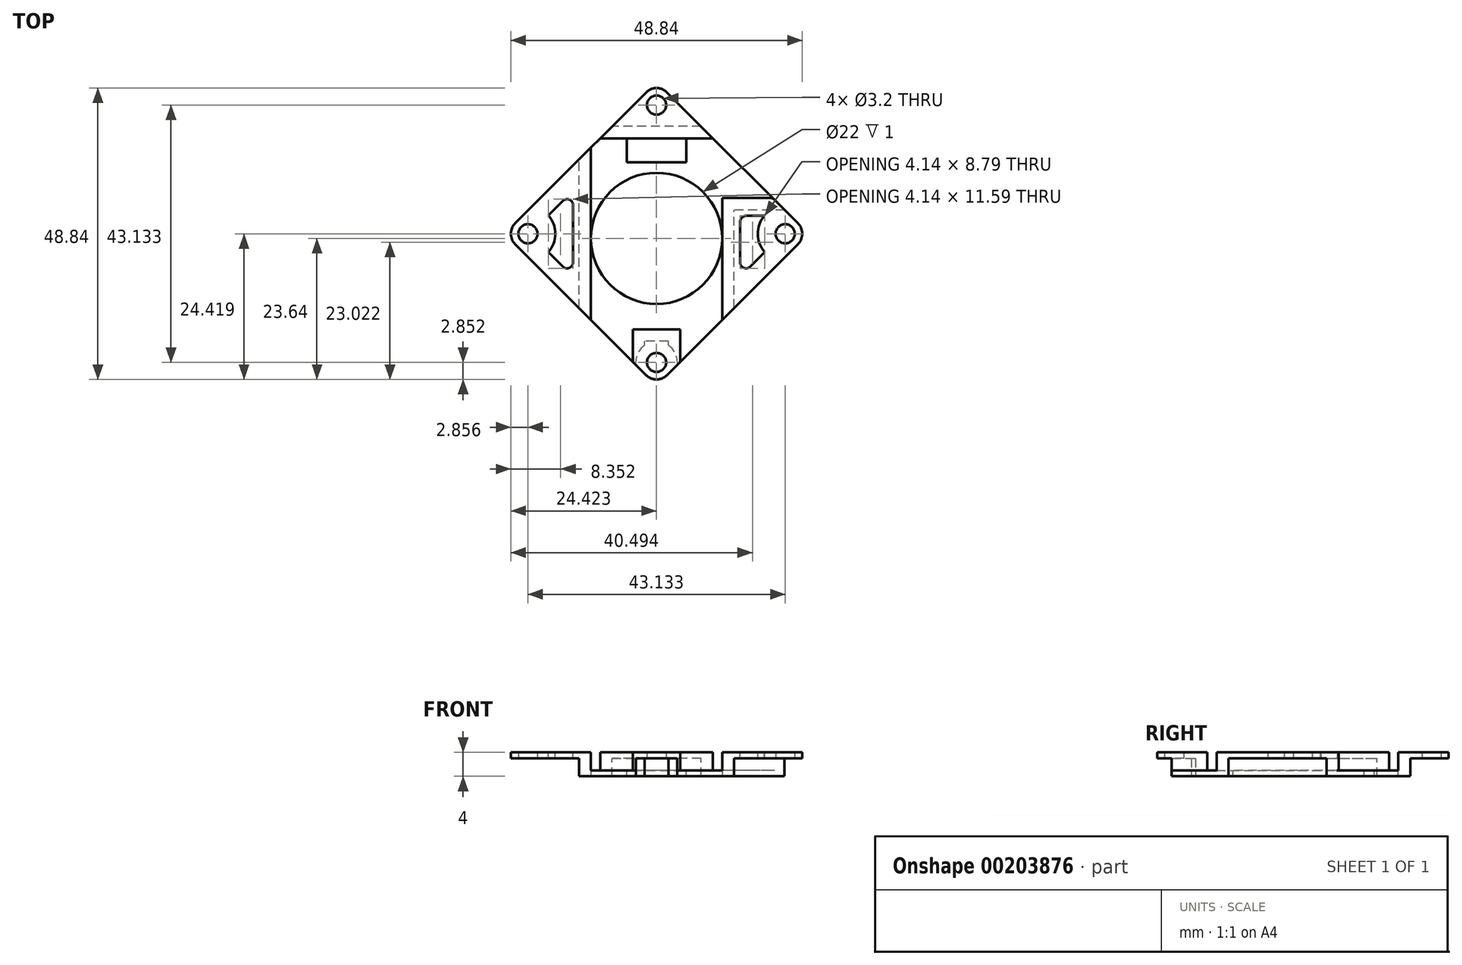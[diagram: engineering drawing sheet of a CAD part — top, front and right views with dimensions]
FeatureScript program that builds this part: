
annotation { "Feature Type Name" : "Feature", "Feature Type Description" : "" }
export const myFeature = defineFeature(function(context is Context, id is Id, definition is map)
    precondition{}
    {
        {
            var Q0;
            Q0=qCreatedBy(makeId("Top.planeOp"),FACE);
            var sketch = newSketch(context, id + "F0", { "sketchPlane" : qUnion([Q0])});
            skLineSegment(sketch, "E0.bottom", {"start": v(16.23, -22.9) * mm, "end": v(-14.77, -22.9) * mm});
            skLineSegment(sketch, "E0.top", {"start": v(16.23, 13.1) * mm, "end": v(-14.77, 13.1) * mm});
            skLineSegment(sketch, "E0.left", {"start": v(18.73, -20.4) * mm, "end": v(18.73, 10.6) * mm});
            skLineSegment(sketch, "E0.right", {"start": v(-17.27, -20.4) * mm, "end": v(-17.27, 10.6) * mm});
            skPoint(sketch, "E0.middle", {"position": v(0.73, -4.9) * mm});
            skCircle(sketch, "E1", {"center": v(-14.52, 10.34) * mm, "radius": 1.6 * mm});
            skPoint(sketch, "E2.visualSharp", {"position": v(-17.27, 13.1) * mm});
            skArc(sketch, "E2.filletArc", {"start": v(-14.77, 13.1) * mm, "mid": v(-16.53, 12.36) * mm, "end": v(-17.27, 10.6) * mm});
            skPoint(sketch, "E3.visualSharp", {"position": v(18.73, 13.1) * mm});
            skArc(sketch, "E3.filletArc", {"start": v(18.73, 10.6) * mm, "mid": v(18, 12.36) * mm, "end": v(16.23, 13.1) * mm});
            skPoint(sketch, "E4.visualSharp", {"position": v(18.73, -22.9) * mm});
            skArc(sketch, "E4.filletArc", {"start": v(16.23, -22.9) * mm, "mid": v(18, -22.18) * mm, "end": v(18.73, -20.4) * mm});
            skPoint(sketch, "E5.visualSharp", {"position": v(-17.27, -22.9) * mm});
            skArc(sketch, "E5.filletArc", {"start": v(-17.27, -20.4) * mm, "mid": v(-16.53, -22.18) * mm, "end": v(-14.77, -22.9) * mm});
            skCircle(sketch, "E6.0.1.0", {"center": v(-14.52, -20.16) * mm, "radius": 1.6 * mm});
            skCircle(sketch, "E6.1.0.0", {"center": v(15.98, 10.34) * mm, "radius": 1.6 * mm});
            skCircle(sketch, "E6.1.1.0", {"center": v(15.98, -20.16) * mm, "radius": 1.6 * mm});
            skLineSegment(sketch, "E6.direction1", {"start": v(-14.52, 10.34) * mm, "end": v(15.98, 10.34) * mm, "construction": true});
            skLineSegment(sketch, "E6.direction2", {"start": v(-14.52, 10.34) * mm, "end": v(-14.52, -20.16) * mm, "construction": true});
            skSolve(sketch);
        }
        {
            var Q0;
            Q0=makeQuery(id+"F0.imprint","IMPRINT",FACE,{"disambiguationData":[TD([[makeQuery(id+"F0.imprint","IMPRINT",EDGE,{"derivedFrom":sQuery(id+"F0.wireOp",EDGE,"E0.bottom")}),-1.0]])]});
            extrude(context, id + "F1", {"entities" : qUnion([Q0]), "depth" : 1 * mm});
        }
        {
            var Q0;
            Q0=makeQuery(id+"F1.opExtrude","SWEPT_BODY",BODY,{"disambiguationData":[OSD([sQuery(id+"F0.wireOp",EDGE,"E0.bottom"),sQuery(id+"F0.wireOp",EDGE,"E0.top"),sQuery(id+"F0.wireOp",EDGE,"E0.left"),sQuery(id+"F0.wireOp",EDGE,"E0.right"),sQuery(id+"F0.wireOp",EDGE,"E1"),sQuery(id+"F0.wireOp",EDGE,"E2.filletArc"),sQuery(id+"F0.wireOp",EDGE,"E3.filletArc"),sQuery(id+"F0.wireOp",EDGE,"E4.filletArc"),sQuery(id+"F0.wireOp",EDGE,"E5.filletArc"),sQuery(id+"F0.wireOp",EDGE,"E6.0.1.0"),sQuery(id+"F0.wireOp",EDGE,"E6.1.0.0"),sQuery(id+"F0.wireOp",EDGE,"E6.1.1.0")])]});
            var Q1;
            Q1=makeQuery(id+"F1.opExtrude","SWEPT_EDGE",EDGE,{"disambiguationData":[OSD([sQuery(id+"F0.wireOp",EDGE,"E0.bottom"),sQuery(id+"F0.wireOp",EDGE,"E4.filletArc")])]});
            transform(context, id + "F2", {"entities" : qUnion([Q0]), "transformType" : TransformType.ROTATION, "transformAxis" : qUnion([Q1]), "angle" : 45 * degree, "makeCopy" : false});
        }
        {
            var Q0;
            Q0=makeQuery(id+"F1.opExtrude","CAP_FACE",FACE,{"disambiguationData":[OSD([sQuery(id+"F0.wireOp",EDGE,"E0.bottom"),sQuery(id+"F0.wireOp",EDGE,"E0.top"),sQuery(id+"F0.wireOp",EDGE,"E0.left"),sQuery(id+"F0.wireOp",EDGE,"E0.right"),sQuery(id+"F0.wireOp",EDGE,"E1"),sQuery(id+"F0.wireOp",EDGE,"E2.filletArc"),sQuery(id+"F0.wireOp",EDGE,"E3.filletArc"),sQuery(id+"F0.wireOp",EDGE,"E4.filletArc"),sQuery(id+"F0.wireOp",EDGE,"E5.filletArc"),sQuery(id+"F0.wireOp",EDGE,"E6.0.1.0"),sQuery(id+"F0.wireOp",EDGE,"E6.1.0.0"),sQuery(id+"F0.wireOp",EDGE,"E6.1.1.0")])],"isStart":false});
            var sketch = newSketch(context, id + "F19", { "sketchPlane" : qUnion([Q0])});
            skLineSegment(sketch, "E7", {"start": v(18, 22.35) * mm, "end": v(18, -20.79) * mm, "construction": true});
            skLineSegment(sketch, "E8", {"start": v(-3.56, 0.78) * mm, "end": v(39.57, 0.78) * mm, "construction": true});
            skLineSegment(sketch, "E9.bottom", {"start": v(31, -17.22) * mm, "end": v(5, -17.22) * mm});
            skLineSegment(sketch, "E9.top", {"start": v(31, 18.78) * mm, "end": v(5, 18.78) * mm});
            skLineSegment(sketch, "E9.left", {"start": v(31, -17.22) * mm, "end": v(31, 18.78) * mm});
            skLineSegment(sketch, "E9.right", {"start": v(5, -17.22) * mm, "end": v(5, 18.78) * mm});
            skPoint(sketch, "E9.middle", {"position": v(18, 0.78) * mm});
            skSolve(sketch);
        }
        {
            var Q0;
            {var subQ6=makeQuery(id+"F1.opExtrude","CAP_EDGE",EDGE,{"disambiguationData":[OSD([sQuery(id+"F0.wireOp",EDGE,"E0.left")])],"isStart":false});var subQ13=sQuery(id+"F19.wireOp",EDGE,"E9.bottom");var subQ14=makeQuery(id+"F19.imprint","INTERSECT",VERTEX,{"derivedFrom":[subQ6,subQ13]});Q0=makeQuery(id+"F19.imprint","IMPRINT",FACE,{"disambiguationData":[TD([[makeQuery(id+"F19.imprint","IMPRINT",EDGE,{"disambiguationData":[TD([[subQ14,-1.0]])],"derivedFrom":subQ13}),-1.0]])]});}
            extrude(context, id + "F3", {"entities" : qUnion([Q0]), "operationType" : NewBodyOperationType.ADD, "oppositeDirection" : true, "depth" : 4 * mm});
        }
        {
            var Q0;
            Q0=makeQuery(id+"F1.opExtrude","CAP_FACE",FACE,{"disambiguationData":[OSD([sQuery(id+"F0.wireOp",EDGE,"E0.bottom"),sQuery(id+"F0.wireOp",EDGE,"E0.top"),sQuery(id+"F0.wireOp",EDGE,"E0.left"),sQuery(id+"F0.wireOp",EDGE,"E0.right"),sQuery(id+"F0.wireOp",EDGE,"E1"),sQuery(id+"F0.wireOp",EDGE,"E2.filletArc"),sQuery(id+"F0.wireOp",EDGE,"E3.filletArc"),sQuery(id+"F0.wireOp",EDGE,"E4.filletArc"),sQuery(id+"F0.wireOp",EDGE,"E5.filletArc"),sQuery(id+"F0.wireOp",EDGE,"E6.0.1.0"),sQuery(id+"F0.wireOp",EDGE,"E6.1.0.0"),sQuery(id+"F0.wireOp",EDGE,"E6.1.1.0")])],"isStart":false});
            var sketch = newSketch(context, id + "F4", { "sketchPlane" : qUnion([Q0])});
            skLineSegment(sketch, "E10", {"start": v(18, 22.35) * mm, "end": v(18, -20.79) * mm, "construction": true});
            skLineSegment(sketch, "E11.bottom", {"start": v(29, -15.22) * mm, "end": v(7, -15.22) * mm});
            skLineSegment(sketch, "E11.top", {"start": v(29, 16.78) * mm, "end": v(7, 16.78) * mm});
            skLineSegment(sketch, "E11.left", {"start": v(29, -15.22) * mm, "end": v(29, 16.78) * mm});
            skLineSegment(sketch, "E11.right", {"start": v(7, -15.22) * mm, "end": v(7, 16.78) * mm});
            skPoint(sketch, "E11.middle", {"position": v(18, 0.78) * mm});
            skSolve(sketch);
        }
        {
            var Q0;
            {var subQ6=makeQuery(id+"F1.opExtrude","CAP_EDGE",EDGE,{"disambiguationData":[OSD([sQuery(id+"F0.wireOp",EDGE,"E0.left")])],"isStart":false});var subQ13=sQuery(id+"F4.wireOp",EDGE,"E11.bottom");var subQ14=makeQuery(id+"F4.imprint","INTERSECT",VERTEX,{"derivedFrom":[subQ6,subQ13]});Q0=makeQuery(id+"F4.imprint","IMPRINT",FACE,{"disambiguationData":[TD([[makeQuery(id+"F4.imprint","IMPRINT",EDGE,{"disambiguationData":[TD([[subQ14,-1.0]])],"derivedFrom":subQ13}),-1.0]])]});}
            extrude(context, id + "F5", {"entities" : qUnion([Q0]), "operationType" : NewBodyOperationType.REMOVE, "oppositeDirection" : true, "depth" : 3 * mm});
        }
        {
            var Q0;
            {var subQ0=sQuery(id+"F0.wireOp",EDGE,"E6.1.1.0");var subQ1=sQuery(id+"F0.wireOp",EDGE,"E4.filletArc");var subQ2=sQuery(id+"F0.wireOp",EDGE,"E0.bottom");var subQ3=sQuery(id+"F0.wireOp",EDGE,"E0.left");Q0=makeQuery(id+"F5.boolean.opBoolean","SPLIT",FACE,{"disambiguationData":[TD([makeQuery(id+"F1.opExtrude","SWEPT_FACE",FACE,{"disambiguationData":[OSD([subQ1])]})])],"derivedFrom":makeQuery(id+"F1.opExtrude","CAP_FACE",FACE,{"disambiguationData":[OSD([subQ2,sQuery(id+"F0.wireOp",EDGE,"E0.top"),subQ3,sQuery(id+"F0.wireOp",EDGE,"E0.right"),sQuery(id+"F0.wireOp",EDGE,"E1"),sQuery(id+"F0.wireOp",EDGE,"E2.filletArc"),sQuery(id+"F0.wireOp",EDGE,"E3.filletArc"),subQ1,sQuery(id+"F0.wireOp",EDGE,"E5.filletArc"),sQuery(id+"F0.wireOp",EDGE,"E6.0.1.0"),sQuery(id+"F0.wireOp",EDGE,"E6.1.0.0"),subQ0])],"isStart":false})});}
            var sketch = newSketch(context, id + "F6", { "sketchPlane" : qUnion([Q0])});
            skLineSegment(sketch, "E12", {"start": v(14, -15.22) * mm, "end": v(14, -20.68) * mm});
            skLineSegment(sketch, "E13", {"start": v(18, -20.79) * mm, "end": v(18, -15.22) * mm, "construction": true});
            skLineSegment(sketch, "E14.MirrorCS", {"start": v(22, -15.22) * mm, "end": v(22, -20.68) * mm});
            skSolve(sketch);
        }
        {
            var Q0;
            {var subQ0=sQuery(id+"F6.wireOp",EDGE,"E12");Q0=makeQuery(id+"F6.imprint","IMPRINT",FACE,{"disambiguationData":[TD([[makeQuery(id+"F6.imprint","IMPRINT",EDGE,{"derivedFrom":subQ0}),-1.0]])]});}
            var Q1;
            {var subQ0=sQuery(id+"F6.wireOp",EDGE,"E14.MirrorCS");Q1=makeQuery(id+"F6.imprint","IMPRINT",FACE,{"disambiguationData":[TD([[makeQuery(id+"F6.imprint","IMPRINT",EDGE,{"derivedFrom":subQ0}),1.0]])]});}
            var Q2;
            Q2=makeQuery(id+"F5.boolean.opBoolean","COPY",FACE,{"derivedFrom":makeQuery(id+"F5.opExtrude","CAP_FACE",FACE,{"disambiguationData":[OSD([sQuery(id+"F0.wireOp",EDGE,"E0.bottom"),sQuery(id+"F0.wireOp",EDGE,"E0.top"),sQuery(id+"F0.wireOp",EDGE,"E0.left"),sQuery(id+"F0.wireOp",EDGE,"E0.right"),sQuery(id+"F4.wireOp",EDGE,"E11.bottom"),sQuery(id+"F4.wireOp",EDGE,"E11.top"),sQuery(id+"F4.wireOp",EDGE,"E11.left"),sQuery(id+"F4.wireOp",EDGE,"E11.right")])],"isStart":false})});
            extrude(context, id + "F20", {"entities" : qUnion([Q0, Q1]), "operationType" : NewBodyOperationType.REMOVE, "endBound" : BoundingType.UP_TO_SURFACE, "oppositeDirection" : true, "endBoundEntityFace" : qUnion([Q2]), "depth" : 25 * mm});
        }
        {
            var Q0;
            Q0=makeQuery(id+"F3.opExtrude","CAP_FACE",FACE,{"disambiguationData":[OSD([sQuery(id+"F0.wireOp",EDGE,"E0.bottom"),sQuery(id+"F0.wireOp",EDGE,"E0.top"),sQuery(id+"F0.wireOp",EDGE,"E0.left"),sQuery(id+"F0.wireOp",EDGE,"E0.right"),sQuery(id+"F19.wireOp",EDGE,"E9.bottom"),sQuery(id+"F19.wireOp",EDGE,"E9.top"),sQuery(id+"F19.wireOp",EDGE,"E9.left"),sQuery(id+"F19.wireOp",EDGE,"E9.right")])],"isStart":false});
            var sketch = newSketch(context, id + "F7", { "sketchPlane" : qUnion([Q0])});
            skLineSegment(sketch, "E15", {"start": v(18, 17.22) * mm, "end": v(18, -18.78) * mm, "construction": true});
            skCircle(sketch, "E16", {"center": v(18, 0) * mm, "radius": 11 * mm});
            skSolve(sketch);
        }
        {
            var Q0;
            Q0=makeQuery(id+"F7.imprint","IMPRINT",FACE,{"disambiguationData":[TD([[makeQuery(id+"F7.imprint","IMPRINT",EDGE,{"derivedFrom":sQuery(id+"F7.wireOp",EDGE,"E16")}),1.0]])]});
            extrude(context, id + "F8", {"entities" : qUnion([Q0]), "operationType" : NewBodyOperationType.REMOVE, "oppositeDirection" : true, "depth" : 25 * mm});
        }
        {
            var Q0;
            {var subQ0=sQuery(id+"F0.wireOp",EDGE,"E6.1.0.0");var subQ1=sQuery(id+"F0.wireOp",EDGE,"E0.left");var subQ2=sQuery(id+"F0.wireOp",EDGE,"E3.filletArc");var subQ3=sQuery(id+"F0.wireOp",EDGE,"E0.top");Q0=makeQuery(id+"F5.boolean.opBoolean","SPLIT",FACE,{"disambiguationData":[TD([makeQuery(id+"F1.opExtrude","SWEPT_FACE",FACE,{"disambiguationData":[OSD([subQ2])]})])],"derivedFrom":makeQuery(id+"F1.opExtrude","CAP_FACE",FACE,{"disambiguationData":[OSD([sQuery(id+"F0.wireOp",EDGE,"E0.bottom"),subQ3,subQ1,sQuery(id+"F0.wireOp",EDGE,"E0.right"),sQuery(id+"F0.wireOp",EDGE,"E1"),sQuery(id+"F0.wireOp",EDGE,"E2.filletArc"),subQ2,sQuery(id+"F0.wireOp",EDGE,"E4.filletArc"),sQuery(id+"F0.wireOp",EDGE,"E5.filletArc"),sQuery(id+"F0.wireOp",EDGE,"E6.0.1.0"),subQ0,sQuery(id+"F0.wireOp",EDGE,"E6.1.1.0")])],"isStart":false})});}
            var sketch = newSketch(context, id + "F21", { "sketchPlane" : qUnion([Q0])});
            skLineSegment(sketch, "E17", {"start": v(29, 6.78) * mm, "end": v(37.46, 6.78) * mm});
            skSolve(sketch);
        }
        {
            var Q0;
            {var subQ0=sQuery(id+"F21.wireOp",EDGE,"E17");Q0=makeQuery(id+"F21.imprint","IMPRINT",FACE,{"disambiguationData":[TD([[makeQuery(id+"F21.imprint","IMPRINT",EDGE,{"derivedFrom":subQ0}),1.0]])]});}
            var Q1;
            {var subQ0=sQuery(id+"F4.wireOp",EDGE,"E11.bottom");var subQ1=sQuery(id+"F0.wireOp",EDGE,"E0.bottom");var subQ2=sQuery(id+"F4.wireOp",EDGE,"E11.right");var subQ3=sQuery(id+"F4.wireOp",EDGE,"E11.left");var subQ4=sQuery(id+"F4.wireOp",EDGE,"E11.top");var subQ5=sQuery(id+"F0.wireOp",EDGE,"E0.right");var subQ6=sQuery(id+"F0.wireOp",EDGE,"E0.left");var subQ7=sQuery(id+"F0.wireOp",EDGE,"E0.top");var subQ8=makeQuery(id+"F20.opExtrude","CAP_FACE",FACE,{"disambiguationData":[OSD([subQ1,subQ7,subQ6,subQ5,subQ0,subQ4,subQ3,subQ2]),ownerDisambiguation([makeQuery(id+"F20.opExtrude","SWEPT_BODY",BODY,{"disambiguationData":[OSD([subQ1,subQ0,sQuery(id+"F6.wireOp",EDGE,"E12")])]})])],"isStart":false});var subQ9=makeQuery(id+"F20.opExtrude","CAP_FACE",FACE,{"disambiguationData":[OSD([subQ1,subQ7,subQ6,subQ5,subQ0,subQ4,subQ3,subQ2]),ownerDisambiguation([makeQuery(id+"F20.opExtrude","SWEPT_BODY",BODY,{"disambiguationData":[OSD([subQ6,subQ0,sQuery(id+"F6.wireOp",EDGE,"E14.MirrorCS")])]})])],"isStart":false});var subQ10=makeQuery(id+"F5.boolean.opBoolean","COPY",FACE,{"derivedFrom":makeQuery(id+"F5.opExtrude","CAP_FACE",FACE,{"disambiguationData":[OSD([subQ1,subQ7,subQ6,subQ5,subQ0,subQ4,subQ3,subQ2])],"isStart":false})});Q1=makeQuery(id+"F8.boolean.opBoolean","SPLIT",FACE,{"disambiguationData":[TD([makeQuery(id+"F1.opExtrude","SWEPT_FACE",FACE,{"disambiguationData":[OSD([subQ7])]})])],"derivedFrom":makeQuery(id+"F20.boolean.opBoolean","MERGE",FACE,{"derivedFrom":[subQ10,subQ8,subQ9]})});}
            extrude(context, id + "F9", {"entities" : qUnion([Q0]), "operationType" : NewBodyOperationType.REMOVE, "endBound" : BoundingType.UP_TO_SURFACE, "oppositeDirection" : true, "endBoundEntityFace" : qUnion([Q1]), "depth" : 25 * mm});
        }
        {
            var Q0;
            {var subQ0=sQuery(id+"F4.wireOp",EDGE,"E11.left");var subQ1=sQuery(id+"F0.wireOp",EDGE,"E0.top");var subQ2=sQuery(id+"F4.wireOp",EDGE,"E11.bottom");var subQ3=sQuery(id+"F0.wireOp",EDGE,"E0.bottom");var subQ4=sQuery(id+"F4.wireOp",EDGE,"E11.right");var subQ5=sQuery(id+"F4.wireOp",EDGE,"E11.top");var subQ6=sQuery(id+"F0.wireOp",EDGE,"E0.right");var subQ7=sQuery(id+"F0.wireOp",EDGE,"E0.left");var subQ8=makeQuery(id+"F20.opExtrude","CAP_FACE",FACE,{"disambiguationData":[OSD([subQ3,subQ1,subQ7,subQ6,subQ2,subQ5,subQ0,subQ4]),ownerDisambiguation([makeQuery(id+"F20.opExtrude","SWEPT_BODY",BODY,{"disambiguationData":[OSD([subQ3,subQ2,sQuery(id+"F6.wireOp",EDGE,"E12")])]})])],"isStart":false});var subQ9=makeQuery(id+"F20.opExtrude","CAP_FACE",FACE,{"disambiguationData":[OSD([subQ3,subQ1,subQ7,subQ6,subQ2,subQ5,subQ0,subQ4]),ownerDisambiguation([makeQuery(id+"F20.opExtrude","SWEPT_BODY",BODY,{"disambiguationData":[OSD([subQ7,subQ2,sQuery(id+"F6.wireOp",EDGE,"E14.MirrorCS")])]})])],"isStart":false});var subQ10=makeQuery(id+"F5.boolean.opBoolean","COPY",FACE,{"derivedFrom":makeQuery(id+"F5.opExtrude","CAP_FACE",FACE,{"disambiguationData":[OSD([subQ3,subQ1,subQ7,subQ6,subQ2,subQ5,subQ0,subQ4])],"isStart":false})});Q0=makeQuery(id+"F9.boolean.opBoolean","MERGE",FACE,{"derivedFrom":[makeQuery(id+"F8.boolean.opBoolean","SPLIT",FACE,{"disambiguationData":[TD([makeQuery(id+"F1.opExtrude","SWEPT_FACE",FACE,{"disambiguationData":[OSD([subQ1])]})])],"derivedFrom":makeQuery(id+"F20.boolean.opBoolean","MERGE",FACE,{"derivedFrom":[subQ10,subQ8,subQ9]})}),makeQuery(id+"F9.opExtrude","CAP_FACE",FACE,{"disambiguationData":[OSD([subQ1,subQ0,sQuery(id+"F21.wireOp",EDGE,"E17")])],"isStart":false})]});}
            var sketch = newSketch(context, id + "F10", { "sketchPlane" : qUnion([Q0])});
            skLineSegment(sketch, "E18", {"start": v(18, 16.78) * mm, "end": v(18, 14.78) * mm, "construction": true});
            skPoint(sketch, "E18.endSnap0", {"position": v(18, 16.78) * mm});
            skLineSegment(sketch, "E19.bottom", {"start": v(23, 16.78) * mm, "end": v(13, 16.78) * mm});
            skLineSegment(sketch, "E19.top", {"start": v(23, 12.78) * mm, "end": v(13, 12.78) * mm});
            skLineSegment(sketch, "E19.left", {"start": v(23, 16.78) * mm, "end": v(23, 12.78) * mm});
            skLineSegment(sketch, "E19.right", {"start": v(13, 16.78) * mm, "end": v(13, 12.78) * mm});
            skPoint(sketch, "E19.middle", {"position": v(18, 14.78) * mm});
            skSolve(sketch);
        }
        {
            var Q0;
            Q0=makeQuery(id+"F10.imprint","IMPRINT",FACE,{"disambiguationData":[TD([[makeQuery(id+"F10.imprint","IMPRINT",EDGE,{"derivedFrom":sQuery(id+"F10.wireOp",EDGE,"E19.bottom")}),1.0]])]});
            extrude(context, id + "F11", {"entities" : qUnion([Q0]), "operationType" : NewBodyOperationType.REMOVE, "oppositeDirection" : true, "depth" : 25 * mm});
        }
        {
            var Q0;
            {var subQ0=sQuery(id+"F0.wireOp",EDGE,"E6.0.1.0");var subQ1=sQuery(id+"F0.wireOp",EDGE,"E5.filletArc");var subQ2=sQuery(id+"F0.wireOp",EDGE,"E0.right");var subQ3=sQuery(id+"F0.wireOp",EDGE,"E0.bottom");Q0=makeQuery(id+"F5.boolean.opBoolean","SPLIT",FACE,{"disambiguationData":[TD([makeQuery(id+"F1.opExtrude","SWEPT_FACE",FACE,{"disambiguationData":[OSD([subQ1])]})])],"derivedFrom":makeQuery(id+"F1.opExtrude","CAP_FACE",FACE,{"disambiguationData":[OSD([subQ3,sQuery(id+"F0.wireOp",EDGE,"E0.top"),sQuery(id+"F0.wireOp",EDGE,"E0.left"),subQ2,sQuery(id+"F0.wireOp",EDGE,"E1"),sQuery(id+"F0.wireOp",EDGE,"E2.filletArc"),sQuery(id+"F0.wireOp",EDGE,"E3.filletArc"),sQuery(id+"F0.wireOp",EDGE,"E4.filletArc"),subQ1,subQ0,sQuery(id+"F0.wireOp",EDGE,"E6.1.0.0"),sQuery(id+"F0.wireOp",EDGE,"E6.1.1.0")])],"isStart":false})});}
            var sketch = newSketch(context, id + "F22", { "sketchPlane" : qUnion([Q0])});
            skArc(sketch, "E20", {"start": v(-0.14, -2.3) * mm, "mid": v(1.04, 0.78) * mm, "end": v(-0.14, 3.85) * mm});
            skLineSegment(sketch, "E21.0", {"start": v(2.3, -4.73) * mm, "end": v(-0.14, -2.3) * mm});
            skLineSegment(sketch, "E21.1", {"start": v(4, -4.02) * mm, "end": v(4, 5.58) * mm});
            skLineSegment(sketch, "E21.2", {"start": v(-3.56, 0.43) * mm, "end": v(-3.21, 0.78) * mm});
            skPoint(sketch, "E22.visualSharp", {"position": v(4, 8) * mm});
            skArc(sketch, "E22.filletArc", {"start": v(4, 5.58) * mm, "mid": v(3.39, 6.5) * mm, "end": v(2.3, 6.29) * mm});
            skPoint(sketch, "E23.visualSharp", {"position": v(4, -6.43) * mm});
            skArc(sketch, "E23.filletArc", {"start": v(2.3, -4.73) * mm, "mid": v(3.39, -4.94) * mm, "end": v(4, -4.02) * mm});
            skLineSegment(sketch, "E24.trimOffspring", {"start": v(-0.14, 3.85) * mm, "end": v(2.3, 6.29) * mm});
            skLineSegment(sketch, "E25.trimOffspring", {"start": v(-3.21, 0.78) * mm, "end": v(-3.56, 1.13) * mm});
            skSolve(sketch);
        }
        {
            var Q0;
            {var subQ0=sQuery(id+"F0.wireOp",EDGE,"E6.1.0.0");var subQ1=sQuery(id+"F0.wireOp",EDGE,"E0.left");var subQ2=sQuery(id+"F0.wireOp",EDGE,"E3.filletArc");var subQ3=sQuery(id+"F0.wireOp",EDGE,"E0.top");Q0=makeQuery(id+"F5.boolean.opBoolean","SPLIT",FACE,{"disambiguationData":[TD([makeQuery(id+"F1.opExtrude","SWEPT_FACE",FACE,{"disambiguationData":[OSD([subQ2])]})])],"derivedFrom":makeQuery(id+"F1.opExtrude","CAP_FACE",FACE,{"disambiguationData":[OSD([sQuery(id+"F0.wireOp",EDGE,"E0.bottom"),subQ3,subQ1,sQuery(id+"F0.wireOp",EDGE,"E0.right"),sQuery(id+"F0.wireOp",EDGE,"E1"),sQuery(id+"F0.wireOp",EDGE,"E2.filletArc"),subQ2,sQuery(id+"F0.wireOp",EDGE,"E4.filletArc"),sQuery(id+"F0.wireOp",EDGE,"E5.filletArc"),sQuery(id+"F0.wireOp",EDGE,"E6.0.1.0"),subQ0,sQuery(id+"F0.wireOp",EDGE,"E6.1.1.0")])],"isStart":false})});}
            var sketch = newSketch(context, id + "F12", { "sketchPlane" : qUnion([Q0])});
            skArc(sketch, "E26", {"start": v(36.08, 3.78) * mm, "mid": v(34.97, 0.73) * mm, "end": v(36.14, -2.3) * mm});
            skLineSegment(sketch, "E27.0", {"start": v(33.7, -4.73) * mm, "end": v(36.14, -2.3) * mm});
            skLineSegment(sketch, "E27.1", {"start": v(32, -4.02) * mm, "end": v(32, 2.78) * mm});
            skLineSegment(sketch, "E27.2", {"start": v(33, 3.78) * mm, "end": v(36.08, 3.78) * mm});
            skPoint(sketch, "E28.visualSharp", {"position": v(32, -6.43) * mm});
            skArc(sketch, "E28.filletArc", {"start": v(32, -4.02) * mm, "mid": v(32.62, -4.94) * mm, "end": v(33.7, -4.73) * mm});
            skPoint(sketch, "E29.visualSharp", {"position": v(32, 3.78) * mm});
            skArc(sketch, "E29.filletArc", {"start": v(33, 3.78) * mm, "mid": v(32.3, 3.49) * mm, "end": v(32, 2.78) * mm});
            skSolve(sketch);
        }
        {
            var Q0;
            Q0=makeQuery(id+"F12.imprint","IMPRINT",FACE,{"disambiguationData":[TD([[makeQuery(id+"F12.imprint","IMPRINT",EDGE,{"derivedFrom":sQuery(id+"F12.wireOp",EDGE,"E26")}),-1.0]])]});
            var Q1;
            Q1=makeQuery(id+"F22.imprint","IMPRINT",FACE,{"disambiguationData":[TD([[makeQuery(id+"F22.imprint","IMPRINT",EDGE,{"derivedFrom":sQuery(id+"F22.wireOp",EDGE,"E20")}),-1.0]])]});
            extrude(context, id + "F13", {"entities" : qUnion([Q0, Q1]), "operationType" : NewBodyOperationType.REMOVE, "oppositeDirection" : true, "depth" : 25 * mm});
        }
        {
            var Q0;
            Q0=makeQuery(id+"F3.opExtrude","CAP_FACE",FACE,{"disambiguationData":[OSD([sQuery(id+"F0.wireOp",EDGE,"E0.bottom"),sQuery(id+"F0.wireOp",EDGE,"E0.top"),sQuery(id+"F0.wireOp",EDGE,"E0.left"),sQuery(id+"F0.wireOp",EDGE,"E0.right"),sQuery(id+"F19.wireOp",EDGE,"E9.bottom"),sQuery(id+"F19.wireOp",EDGE,"E9.top"),sQuery(id+"F19.wireOp",EDGE,"E9.left"),sQuery(id+"F19.wireOp",EDGE,"E9.right")])],"isStart":false});
            var sketch = newSketch(context, id + "F23", { "sketchPlane" : qUnion([Q0])});
            skLineSegment(sketch, "E30", {"start": v(10.55, 17.22) * mm, "end": v(14.53, 21.2) * mm});
            skLineSegment(sketch, "E31", {"start": v(16, 17.92) * mm, "end": v(16, 17.22) * mm});
            skLineSegment(sketch, "E32", {"start": v(18, 17.22) * mm, "end": v(18, 28.85) * mm, "construction": true});
            skLineSegment(sketch, "E33.MirrorCS", {"start": v(25.46, 17.22) * mm, "end": v(21.48, 21.2) * mm});
            skLineSegment(sketch, "E34.MirrorCS", {"start": v(20, 17.92) * mm, "end": v(20, 17.22) * mm});
            skArc(sketch, "E35", {"start": v(14.53, 21.2) * mm, "mid": v(14.8, 19.35) * mm, "end": v(16, 17.92) * mm});
            skPoint(sketch, "E36.orphan", {"position": v(16, 22.68) * mm});
            skPoint(sketch, "E37.orphan", {"position": v(20, 22.68) * mm});
            skArc(sketch, "E38.trimOffspring", {"start": v(20, 17.92) * mm, "mid": v(21.2, 19.35) * mm, "end": v(21.48, 21.2) * mm});
            skSolve(sketch);
        }
        {
            var Q0;
            {var subQ0=sQuery(id+"F23.wireOp",EDGE,"E30");Q0=makeQuery(id+"F23.imprint","IMPRINT",FACE,{"disambiguationData":[TD([[makeQuery(id+"F23.imprint","IMPRINT",EDGE,{"derivedFrom":subQ0}),-1.0]])]});}
            var Q1;
            {var subQ0=sQuery(id+"F23.wireOp",EDGE,"E33.MirrorCS");Q1=makeQuery(id+"F23.imprint","IMPRINT",FACE,{"disambiguationData":[TD([[makeQuery(id+"F23.imprint","IMPRINT",EDGE,{"derivedFrom":subQ0}),1.0]])]});}
            var Q2;
            {var subQ0=sQuery(id+"F4.wireOp",EDGE,"E11.left");var subQ1=sQuery(id+"F4.wireOp",EDGE,"E11.right");var subQ2=sQuery(id+"F4.wireOp",EDGE,"E11.top");var subQ3=sQuery(id+"F4.wireOp",EDGE,"E11.bottom");var subQ4=sQuery(id+"F0.wireOp",EDGE,"E0.right");var subQ5=sQuery(id+"F0.wireOp",EDGE,"E0.left");var subQ6=sQuery(id+"F0.wireOp",EDGE,"E0.top");var subQ7=sQuery(id+"F0.wireOp",EDGE,"E0.bottom");var subQ8=makeQuery(id+"F5.boolean.opBoolean","COPY",FACE,{"derivedFrom":makeQuery(id+"F5.opExtrude","CAP_FACE",FACE,{"disambiguationData":[OSD([subQ7,subQ6,subQ5,subQ4,subQ3,subQ2,subQ0,subQ1])],"isStart":false})});var subQ9=sQuery(id+"F6.wireOp",EDGE,"E12");var subQ10=makeQuery(id+"F20.opExtrude","CAP_FACE",FACE,{"disambiguationData":[OSD([subQ7,subQ6,subQ5,subQ4,subQ3,subQ2,subQ0,subQ1]),ownerDisambiguation([makeQuery(id+"F20.opExtrude","SWEPT_BODY",BODY,{"disambiguationData":[OSD([subQ7,subQ3,subQ9])]})])],"isStart":false});var subQ11=sQuery(id+"F6.wireOp",EDGE,"E14.MirrorCS");var subQ12=makeQuery(id+"F20.opExtrude","CAP_FACE",FACE,{"disambiguationData":[OSD([subQ7,subQ6,subQ5,subQ4,subQ3,subQ2,subQ0,subQ1]),ownerDisambiguation([makeQuery(id+"F20.opExtrude","SWEPT_BODY",BODY,{"disambiguationData":[OSD([subQ5,subQ3,subQ11])]})])],"isStart":false});Q2=makeQuery(id+"F8.boolean.opBoolean","SPLIT",FACE,{"disambiguationData":[TD([makeQuery(id+"F1.opExtrude","SWEPT_FACE",FACE,{"disambiguationData":[OSD([subQ7])]})])],"derivedFrom":makeQuery(id+"F20.boolean.opBoolean","MERGE",FACE,{"derivedFrom":[subQ8,subQ10,subQ12]})});}
            extrude(context, id + "F14", {"entities" : qUnion([Q0, Q1]), "operationType" : NewBodyOperationType.ADD, "endBound" : BoundingType.UP_TO_SURFACE, "oppositeDirection" : true, "endBoundEntityFace" : qUnion([Q2]), "depth" : 25 * mm});
        }
        {
            var Q0;
            {var subQ0=sQuery(id+"F19.wireOp",EDGE,"E9.bottom");var subQ1=sQuery(id+"F4.wireOp",EDGE,"E11.left");var subQ2=sQuery(id+"F4.wireOp",EDGE,"E11.right");var subQ3=sQuery(id+"F4.wireOp",EDGE,"E11.top");var subQ4=sQuery(id+"F4.wireOp",EDGE,"E11.bottom");var subQ5=sQuery(id+"F0.wireOp",EDGE,"E0.right");var subQ6=sQuery(id+"F0.wireOp",EDGE,"E0.left");var subQ7=sQuery(id+"F0.wireOp",EDGE,"E0.top");var subQ8=sQuery(id+"F0.wireOp",EDGE,"E0.bottom");var subQ9=makeQuery(id+"F5.boolean.opBoolean","COPY",FACE,{"derivedFrom":makeQuery(id+"F5.opExtrude","CAP_FACE",FACE,{"disambiguationData":[OSD([subQ8,subQ7,subQ6,subQ5,subQ4,subQ3,subQ1,subQ2])],"isStart":false})});var subQ10=sQuery(id+"F6.wireOp",EDGE,"E12");var subQ11=makeQuery(id+"F20.opExtrude","CAP_FACE",FACE,{"disambiguationData":[OSD([subQ8,subQ7,subQ6,subQ5,subQ4,subQ3,subQ1,subQ2]),ownerDisambiguation([makeQuery(id+"F20.opExtrude","SWEPT_BODY",BODY,{"disambiguationData":[OSD([subQ8,subQ4,subQ10])]})])],"isStart":false});var subQ12=sQuery(id+"F6.wireOp",EDGE,"E14.MirrorCS");var subQ13=makeQuery(id+"F20.opExtrude","CAP_FACE",FACE,{"disambiguationData":[OSD([subQ8,subQ7,subQ6,subQ5,subQ4,subQ3,subQ1,subQ2]),ownerDisambiguation([makeQuery(id+"F20.opExtrude","SWEPT_BODY",BODY,{"disambiguationData":[OSD([subQ6,subQ4,subQ12])]})])],"isStart":false});Q0=makeQuery(id+"F14.boolean.opBoolean","MERGE",FACE,{"derivedFrom":[makeQuery(id+"F8.boolean.opBoolean","SPLIT",FACE,{"disambiguationData":[TD([makeQuery(id+"F1.opExtrude","SWEPT_FACE",FACE,{"disambiguationData":[OSD([subQ8])]})])],"derivedFrom":makeQuery(id+"F20.boolean.opBoolean","MERGE",FACE,{"derivedFrom":[subQ9,subQ11,subQ13]})}),makeQuery(id+"F14.opExtrude","CAP_FACE",FACE,{"disambiguationData":[OSD([subQ0,sQuery(id+"F23.wireOp",EDGE,"E30"),sQuery(id+"F23.wireOp",EDGE,"E31"),sQuery(id+"F23.wireOp",EDGE,"E35")])],"isStart":false}),makeQuery(id+"F14.opExtrude","CAP_FACE",FACE,{"disambiguationData":[OSD([subQ0,sQuery(id+"F23.wireOp",EDGE,"E33.MirrorCS"),sQuery(id+"F23.wireOp",EDGE,"E34.MirrorCS"),sQuery(id+"F23.wireOp",EDGE,"E38.trimOffspring")])],"isStart":false})]});}
            var sketch = newSketch(context, id + "F24", { "sketchPlane" : qUnion([Q0])});
            skLineSegment(sketch, "E39", {"start": v(14, -17.22) * mm, "end": v(14, -20.68) * mm});
            skLineSegment(sketch, "E40", {"start": v(22, -17.22) * mm, "end": v(22, -20.68) * mm});
            skSolve(sketch);
        }
        {
            var Q0;
            {var subQ6=sQuery(id+"F24.wireOp",EDGE,"E40");Q0=makeQuery(id+"F24.imprint","IMPRINT",FACE,{"disambiguationData":[TD([[makeQuery(id+"F24.imprint","IMPRINT",EDGE,{"derivedFrom":subQ6}),-1.0]])]});}
            var Q1;
            {var subQ13=sQuery(id+"F24.wireOp",EDGE,"E39");Q1=makeQuery(id+"F24.imprint","IMPRINT",FACE,{"disambiguationData":[TD([[makeQuery(id+"F24.imprint","IMPRINT",EDGE,{"derivedFrom":subQ13}),1.0]])]});}
            var Q2;
            {var subQ0=sQuery(id+"F0.wireOp",EDGE,"E6.1.1.0");var subQ1=sQuery(id+"F0.wireOp",EDGE,"E4.filletArc");var subQ2=sQuery(id+"F0.wireOp",EDGE,"E0.bottom");var subQ3=sQuery(id+"F0.wireOp",EDGE,"E0.left");Q2=makeQuery(id+"F3.boolean.opBoolean","SPLIT",FACE,{"disambiguationData":[TD([makeQuery(id+"F1.opExtrude","SWEPT_FACE",FACE,{"disambiguationData":[OSD([subQ1])]})])],"derivedFrom":makeQuery(id+"F1.opExtrude","CAP_FACE",FACE,{"disambiguationData":[OSD([subQ2,sQuery(id+"F0.wireOp",EDGE,"E0.top"),subQ3,sQuery(id+"F0.wireOp",EDGE,"E0.right"),sQuery(id+"F0.wireOp",EDGE,"E1"),sQuery(id+"F0.wireOp",EDGE,"E2.filletArc"),sQuery(id+"F0.wireOp",EDGE,"E3.filletArc"),subQ1,sQuery(id+"F0.wireOp",EDGE,"E5.filletArc"),sQuery(id+"F0.wireOp",EDGE,"E6.0.1.0"),sQuery(id+"F0.wireOp",EDGE,"E6.1.0.0"),subQ0])],"isStart":true})});}
            extrude(context, id + "F15", {"entities" : qUnion([Q0, Q1]), "operationType" : NewBodyOperationType.ADD, "endBound" : BoundingType.UP_TO_SURFACE, "endBoundEntityFace" : qUnion([Q2]), "depth" : 25 * mm});
        }
        {
            var Q0;
            {var subQ0=sQuery(id+"F19.wireOp",EDGE,"E9.bottom");Q0=makeQuery(id+"F14.boolean.opBoolean","MERGE",FACE,{"derivedFrom":[makeQuery(id+"F3.opExtrude","CAP_FACE",FACE,{"disambiguationData":[OSD([sQuery(id+"F0.wireOp",EDGE,"E0.bottom"),sQuery(id+"F0.wireOp",EDGE,"E0.top"),sQuery(id+"F0.wireOp",EDGE,"E0.left"),sQuery(id+"F0.wireOp",EDGE,"E0.right"),subQ0,sQuery(id+"F19.wireOp",EDGE,"E9.top"),sQuery(id+"F19.wireOp",EDGE,"E9.left"),sQuery(id+"F19.wireOp",EDGE,"E9.right")])],"isStart":false}),makeQuery(id+"F14.opExtrude","CAP_FACE",FACE,{"disambiguationData":[OSD([subQ0,sQuery(id+"F23.wireOp",EDGE,"E30"),sQuery(id+"F23.wireOp",EDGE,"E31"),sQuery(id+"F23.wireOp",EDGE,"E35")])],"isStart":true}),makeQuery(id+"F14.opExtrude","CAP_FACE",FACE,{"disambiguationData":[OSD([subQ0,sQuery(id+"F23.wireOp",EDGE,"E33.MirrorCS"),sQuery(id+"F23.wireOp",EDGE,"E34.MirrorCS"),sQuery(id+"F23.wireOp",EDGE,"E38.trimOffspring")])],"isStart":true})]});}
            var sketch = newSketch(context, id + "F25", { "sketchPlane" : qUnion([Q0])});
            skLineSegment(sketch, "E41", {"start": v(31, -13.23) * mm, "end": v(39.46, -4.78) * mm});
            skLineSegment(sketch, "E42", {"start": v(39.46, -4.78) * mm, "end": v(31, -4.78) * mm});
            skSolve(sketch);
        }
        {
            var Q0;
            {var subQ0=sQuery(id+"F25.wireOp",EDGE,"E41");Q0=makeQuery(id+"F25.imprint","IMPRINT",FACE,{"disambiguationData":[TD([[makeQuery(id+"F25.imprint","IMPRINT",EDGE,{"derivedFrom":subQ0}),1.0]])]});}
            var Q1;
            {var subQ0=sQuery(id+"F4.wireOp",EDGE,"E11.left");var subQ1=sQuery(id+"F0.wireOp",EDGE,"E0.top");var subQ2=sQuery(id+"F4.wireOp",EDGE,"E11.bottom");var subQ3=sQuery(id+"F0.wireOp",EDGE,"E0.bottom");var subQ4=sQuery(id+"F4.wireOp",EDGE,"E11.right");var subQ5=sQuery(id+"F4.wireOp",EDGE,"E11.top");var subQ6=sQuery(id+"F0.wireOp",EDGE,"E0.right");var subQ7=sQuery(id+"F0.wireOp",EDGE,"E0.left");var subQ8=makeQuery(id+"F20.opExtrude","CAP_FACE",FACE,{"disambiguationData":[OSD([subQ3,subQ1,subQ7,subQ6,subQ2,subQ5,subQ0,subQ4]),ownerDisambiguation([makeQuery(id+"F20.opExtrude","SWEPT_BODY",BODY,{"disambiguationData":[OSD([subQ3,subQ2,sQuery(id+"F6.wireOp",EDGE,"E12")])]})])],"isStart":false});var subQ9=makeQuery(id+"F20.opExtrude","CAP_FACE",FACE,{"disambiguationData":[OSD([subQ3,subQ1,subQ7,subQ6,subQ2,subQ5,subQ0,subQ4]),ownerDisambiguation([makeQuery(id+"F20.opExtrude","SWEPT_BODY",BODY,{"disambiguationData":[OSD([subQ7,subQ2,sQuery(id+"F6.wireOp",EDGE,"E14.MirrorCS")])]})])],"isStart":false});var subQ10=makeQuery(id+"F5.boolean.opBoolean","COPY",FACE,{"derivedFrom":makeQuery(id+"F5.opExtrude","CAP_FACE",FACE,{"disambiguationData":[OSD([subQ3,subQ1,subQ7,subQ6,subQ2,subQ5,subQ0,subQ4])],"isStart":false})});Q1=makeQuery(id+"F9.boolean.opBoolean","MERGE",FACE,{"derivedFrom":[makeQuery(id+"F8.boolean.opBoolean","SPLIT",FACE,{"disambiguationData":[TD([makeQuery(id+"F1.opExtrude","SWEPT_FACE",FACE,{"disambiguationData":[OSD([subQ1])]})])],"derivedFrom":makeQuery(id+"F20.boolean.opBoolean","MERGE",FACE,{"derivedFrom":[subQ10,subQ8,subQ9]})}),makeQuery(id+"F9.opExtrude","CAP_FACE",FACE,{"disambiguationData":[OSD([subQ1,subQ0,sQuery(id+"F21.wireOp",EDGE,"E17")])],"isStart":false})]});}
            extrude(context, id + "F16", {"entities" : qUnion([Q0]), "operationType" : NewBodyOperationType.ADD, "endBound" : BoundingType.UP_TO_SURFACE, "oppositeDirection" : true, "endBoundEntityFace" : qUnion([Q1]), "depth" : 25 * mm});
        }
        {
            var Q0;
            {var subQ0=sQuery(id+"F4.wireOp",EDGE,"E11.left");var subQ1=sQuery(id+"F0.wireOp",EDGE,"E0.top");var subQ2=sQuery(id+"F4.wireOp",EDGE,"E11.bottom");var subQ3=sQuery(id+"F0.wireOp",EDGE,"E0.bottom");var subQ4=sQuery(id+"F4.wireOp",EDGE,"E11.right");var subQ5=sQuery(id+"F4.wireOp",EDGE,"E11.top");var subQ6=sQuery(id+"F0.wireOp",EDGE,"E0.right");var subQ7=sQuery(id+"F0.wireOp",EDGE,"E0.left");var subQ8=makeQuery(id+"F20.opExtrude","CAP_FACE",FACE,{"disambiguationData":[OSD([subQ3,subQ1,subQ7,subQ6,subQ2,subQ5,subQ0,subQ4]),ownerDisambiguation([makeQuery(id+"F20.opExtrude","SWEPT_BODY",BODY,{"disambiguationData":[OSD([subQ3,subQ2,sQuery(id+"F6.wireOp",EDGE,"E12")])]})])],"isStart":false});var subQ9=makeQuery(id+"F20.opExtrude","CAP_FACE",FACE,{"disambiguationData":[OSD([subQ3,subQ1,subQ7,subQ6,subQ2,subQ5,subQ0,subQ4]),ownerDisambiguation([makeQuery(id+"F20.opExtrude","SWEPT_BODY",BODY,{"disambiguationData":[OSD([subQ7,subQ2,sQuery(id+"F6.wireOp",EDGE,"E14.MirrorCS")])]})])],"isStart":false});var subQ10=makeQuery(id+"F5.boolean.opBoolean","COPY",FACE,{"derivedFrom":makeQuery(id+"F5.opExtrude","CAP_FACE",FACE,{"disambiguationData":[OSD([subQ3,subQ1,subQ7,subQ6,subQ2,subQ5,subQ0,subQ4])],"isStart":false})});Q0=makeQuery(id+"F16.boolean.opBoolean","MERGE",FACE,{"derivedFrom":[makeQuery(id+"F9.boolean.opBoolean","MERGE",FACE,{"derivedFrom":[makeQuery(id+"F8.boolean.opBoolean","SPLIT",FACE,{"disambiguationData":[TD([makeQuery(id+"F1.opExtrude","SWEPT_FACE",FACE,{"disambiguationData":[OSD([subQ1])]})])],"derivedFrom":makeQuery(id+"F20.boolean.opBoolean","MERGE",FACE,{"derivedFrom":[subQ10,subQ8,subQ9]})}),makeQuery(id+"F9.opExtrude","CAP_FACE",FACE,{"disambiguationData":[OSD([subQ1,subQ0,sQuery(id+"F21.wireOp",EDGE,"E17")])],"isStart":false})]}),makeQuery(id+"F16.opExtrude","CAP_FACE",FACE,{"disambiguationData":[OSD([sQuery(id+"F19.wireOp",EDGE,"E9.left"),sQuery(id+"F25.wireOp",EDGE,"E41"),sQuery(id+"F25.wireOp",EDGE,"E42")])],"isStart":false})]});}
            var sketch = newSketch(context, id + "F26", { "sketchPlane" : qUnion([Q0])});
            skLineSegment(sketch, "E43", {"start": v(31, 6.78) * mm, "end": v(37.46, 6.78) * mm});
            skSolve(sketch);
        }
        {
            var Q0;
            {var subQ0=sQuery(id+"F26.wireOp",EDGE,"E43");Q0=makeQuery(id+"F26.imprint","IMPRINT",FACE,{"disambiguationData":[TD([[makeQuery(id+"F26.imprint","IMPRINT",EDGE,{"derivedFrom":subQ0}),-1.0]])]});}
            var Q1;
            {var subQ0=sQuery(id+"F0.wireOp",EDGE,"E6.1.0.0");var subQ1=sQuery(id+"F0.wireOp",EDGE,"E0.left");var subQ2=sQuery(id+"F0.wireOp",EDGE,"E3.filletArc");var subQ3=sQuery(id+"F0.wireOp",EDGE,"E0.top");Q1=makeQuery(id+"F3.boolean.opBoolean","SPLIT",FACE,{"disambiguationData":[TD([makeQuery(id+"F1.opExtrude","SWEPT_FACE",FACE,{"disambiguationData":[OSD([subQ2])]})])],"derivedFrom":makeQuery(id+"F1.opExtrude","CAP_FACE",FACE,{"disambiguationData":[OSD([sQuery(id+"F0.wireOp",EDGE,"E0.bottom"),subQ3,subQ1,sQuery(id+"F0.wireOp",EDGE,"E0.right"),sQuery(id+"F0.wireOp",EDGE,"E1"),sQuery(id+"F0.wireOp",EDGE,"E2.filletArc"),subQ2,sQuery(id+"F0.wireOp",EDGE,"E4.filletArc"),sQuery(id+"F0.wireOp",EDGE,"E5.filletArc"),sQuery(id+"F0.wireOp",EDGE,"E6.0.1.0"),subQ0,sQuery(id+"F0.wireOp",EDGE,"E6.1.1.0")])],"isStart":true})});}
            extrude(context, id + "F17", {"entities" : qUnion([Q0]), "operationType" : NewBodyOperationType.ADD, "endBound" : BoundingType.UP_TO_SURFACE, "endBoundEntityFace" : qUnion([Q1]), "depth" : 25 * mm});
        }
        {
            var Q0;
            Q0=makeQuery(id+"F20.boolean.opBoolean","COPY",EDGE,{"derivedFrom":makeQuery(id+"F20.opExtrude","SWEPT_EDGE",EDGE,{"disambiguationData":[OSD([sQuery(id+"F4.wireOp",EDGE,"E11.bottom"),sQuery(id+"F6.wireOp",EDGE,"E14.MirrorCS")])]})});
            var Q1;
            Q1=makeQuery(id+"F20.boolean.opBoolean","COPY",EDGE,{"derivedFrom":makeQuery(id+"F20.opExtrude","SWEPT_EDGE",EDGE,{"disambiguationData":[OSD([sQuery(id+"F4.wireOp",EDGE,"E11.bottom"),sQuery(id+"F6.wireOp",EDGE,"E12")])]})});
            var Q2;
            Q2=makeQuery(id+"F5.boolean.opBoolean","COPY",EDGE,{"derivedFrom":makeQuery(id+"F5.opExtrude","SWEPT_EDGE",EDGE,{"disambiguationData":[OSD([sQuery(id+"F0.wireOp",EDGE,"E0.bottom"),sQuery(id+"F4.wireOp",EDGE,"E11.right")])]})});
            var Q3;
            {var subQ0=sQuery(id+"F0.wireOp",EDGE,"E0.bottom");Q3=makeQuery(id+"F15.boolean.opBoolean","MERGE",EDGE,{"derivedFrom":[makeQuery(id+"F20.boolean.opBoolean","COPY",EDGE,{"derivedFrom":makeQuery(id+"F20.opExtrude","SWEPT_EDGE",EDGE,{"disambiguationData":[OSD([subQ0,sQuery(id+"F6.wireOp",EDGE,"E12")])]})}),makeQuery(id+"F15.opExtrude","SWEPT_EDGE",EDGE,{"disambiguationData":[OSD([subQ0,sQuery(id+"F0.wireOp",EDGE,"E0.top"),sQuery(id+"F0.wireOp",EDGE,"E0.left"),sQuery(id+"F0.wireOp",EDGE,"E0.right"),sQuery(id+"F4.wireOp",EDGE,"E11.bottom"),sQuery(id+"F4.wireOp",EDGE,"E11.top"),sQuery(id+"F4.wireOp",EDGE,"E11.left"),sQuery(id+"F4.wireOp",EDGE,"E11.right"),sQuery(id+"F23.wireOp",EDGE,"E30"),sQuery(id+"F24.wireOp",EDGE,"E39")])]})]});}
            var Q4;
            {var subQ0=sQuery(id+"F0.wireOp",EDGE,"E0.left");Q4=makeQuery(id+"F15.boolean.opBoolean","MERGE",EDGE,{"derivedFrom":[makeQuery(id+"F20.boolean.opBoolean","COPY",EDGE,{"derivedFrom":makeQuery(id+"F20.opExtrude","SWEPT_EDGE",EDGE,{"disambiguationData":[OSD([subQ0,sQuery(id+"F6.wireOp",EDGE,"E14.MirrorCS")])]})}),makeQuery(id+"F15.opExtrude","SWEPT_EDGE",EDGE,{"disambiguationData":[OSD([sQuery(id+"F0.wireOp",EDGE,"E0.bottom"),sQuery(id+"F0.wireOp",EDGE,"E0.top"),subQ0,sQuery(id+"F0.wireOp",EDGE,"E0.right"),sQuery(id+"F4.wireOp",EDGE,"E11.bottom"),sQuery(id+"F4.wireOp",EDGE,"E11.top"),sQuery(id+"F4.wireOp",EDGE,"E11.left"),sQuery(id+"F4.wireOp",EDGE,"E11.right"),sQuery(id+"F23.wireOp",EDGE,"E33.MirrorCS"),sQuery(id+"F24.wireOp",EDGE,"E40")])]})]});}
            var Q5;
            Q5=makeQuery(id+"F5.boolean.opBoolean","COPY",EDGE,{"derivedFrom":makeQuery(id+"F5.opExtrude","SWEPT_EDGE",EDGE,{"disambiguationData":[OSD([sQuery(id+"F0.wireOp",EDGE,"E0.left"),sQuery(id+"F4.wireOp",EDGE,"E11.left")])]})});
            var Q6;
            {var subQ0=sQuery(id+"F0.wireOp",EDGE,"E0.top");Q6=makeQuery(id+"F17.boolean.opBoolean","MERGE",EDGE,{"derivedFrom":[makeQuery(id+"F9.boolean.opBoolean","COPY",EDGE,{"derivedFrom":makeQuery(id+"F9.opExtrude","SWEPT_EDGE",EDGE,{"disambiguationData":[OSD([subQ0,sQuery(id+"F21.wireOp",EDGE,"E17")])]})}),makeQuery(id+"F17.opExtrude","SWEPT_EDGE",EDGE,{"disambiguationData":[OSD([subQ0,sQuery(id+"F25.wireOp",EDGE,"E41"),sQuery(id+"F26.wireOp",EDGE,"E43")])]})]});}
            var Q7;
            Q7=makeQuery(id+"F9.boolean.opBoolean","COPY",EDGE,{"derivedFrom":makeQuery(id+"F9.opExtrude","SWEPT_EDGE",EDGE,{"disambiguationData":[OSD([sQuery(id+"F4.wireOp",EDGE,"E11.left"),sQuery(id+"F21.wireOp",EDGE,"E17")])]})});
            var Q8;
            Q8=makeQuery(id+"F5.boolean.opBoolean","COPY",EDGE,{"derivedFrom":makeQuery(id+"F5.opExtrude","SWEPT_EDGE",EDGE,{"disambiguationData":[OSD([sQuery(id+"F0.wireOp",EDGE,"E0.top"),sQuery(id+"F4.wireOp",EDGE,"E11.top")])]})});
            var Q9;
            Q9=makeQuery(id+"F5.boolean.opBoolean","COPY",EDGE,{"derivedFrom":makeQuery(id+"F5.opExtrude","SWEPT_EDGE",EDGE,{"disambiguationData":[OSD([sQuery(id+"F0.wireOp",EDGE,"E0.right"),sQuery(id+"F4.wireOp",EDGE,"E11.top")])]})});
            var Q10;
            Q10=makeQuery(id+"F5.boolean.opBoolean","COPY",EDGE,{"derivedFrom":makeQuery(id+"F5.opExtrude","SWEPT_EDGE",EDGE,{"disambiguationData":[OSD([sQuery(id+"F0.wireOp",EDGE,"E0.right"),sQuery(id+"F4.wireOp",EDGE,"E11.right")])]})});
            fillet(context, id + "F18", {"entities" : qUnion([Q0, Q1, Q2, Q3, Q4, Q5, Q6, Q7, Q8, Q9, Q10]), "radius" : 1 * mm, "tangentPropagation" : true, "allowEdgeOverflow" : false});
        }
    });
